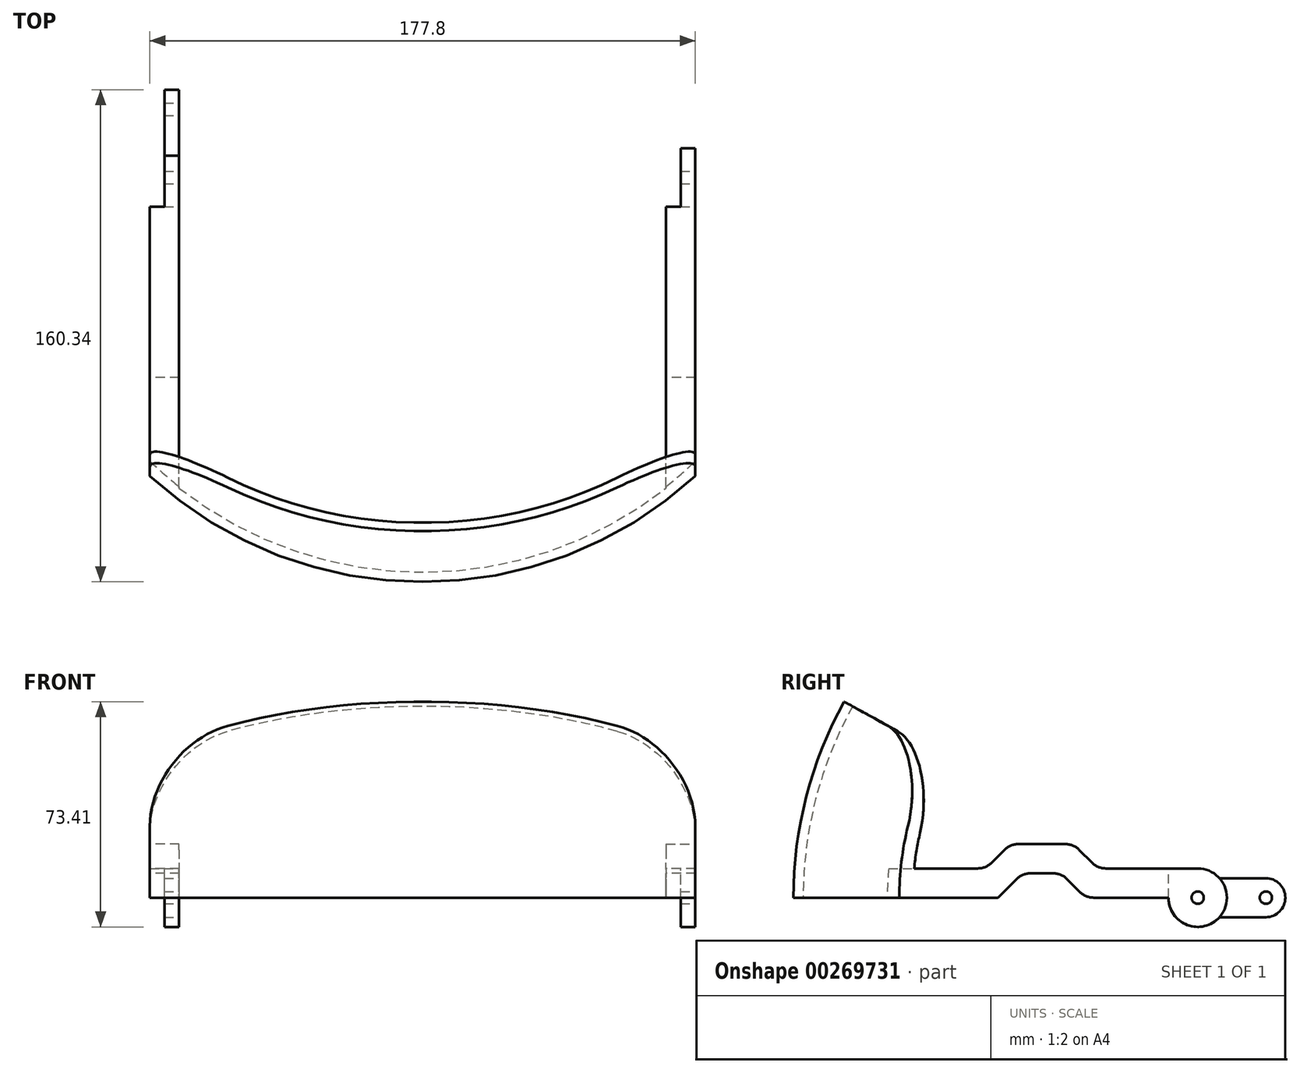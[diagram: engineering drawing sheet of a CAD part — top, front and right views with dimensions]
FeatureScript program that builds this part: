
annotation { "Feature Type Name" : "Feature", "Feature Type Description" : "" }
export const myFeature = defineFeature(function(context is Context, id is Id, definition is map)
    precondition{}
    {
        {
            var Q0;
            Q0=qCreatedBy(makeId("Right.planeOp"),FACE);
            var sketch = newSketch(context, id + "F0", { "sketchPlane" : qUnion([Q0])});
            skArc(sketch, "E0", {"start": v(0, 131.76) * mm, "mid": v(-131.76, 0) * mm, "end": v(0, -131.76) * mm});
            skArc(sketch, "E1", {"start": v(0, 128.59) * mm, "mid": v(-128.59, 0) * mm, "end": v(0, -128.59) * mm});
            skLineSegment(sketch, "E2", {"start": v(0, 131.76) * mm, "end": v(0, 128.59) * mm});
            skLineSegment(sketch, "E3.trimOffspring", {"start": v(0, 0) * mm, "end": v(0, -131.76) * mm});
            skPoint(sketch, "E4.orphan", {"position": v(0, 135.47) * mm});
            skSolve(sketch);
        }
        {
            var Q0;
            Q0 = qSketchRegion(id + "F0", true);
            var Q1;
            Q1=sQuery(id+"F0.wireOp",EDGE,"E3.trimOffspring");
            revolve(context, id + "F1", {"entities" : qUnion([Q0]), "axis" : qUnion([Q1]), "revolveType" : RevolveType.FULL});
        }
        {
            var Q0;
            Q0=qCreatedBy(makeId("Front.planeOp"),FACE);
            var sketch = newSketch(context, id + "F2", { "sketchPlane" : qUnion([Q0])});
            skLineSegment(sketch, "E5.left", {"start": v(88.9, 152.6) * mm, "end": v(88.9, -152.6) * mm});
            skLineSegment(sketch, "E5.right", {"start": v(-88.9, 152.6) * mm, "end": v(-88.9, -152.6) * mm});
            skPoint(sketch, "E5.middle", {"position": v(0, 0) * mm});
            skLineSegment(sketch, "E6.bottom", {"start": v(230.94, 152.6) * mm, "end": v(88.9, 152.6) * mm});
            skLineSegment(sketch, "E6.top", {"start": v(230.94, -152.6) * mm, "end": v(88.9, -152.6) * mm});
            skLineSegment(sketch, "E6.left", {"start": v(230.94, 152.6) * mm, "end": v(230.94, -152.6) * mm});
            skLineSegment(sketch, "E6.right", {"start": v(-230.94, 152.6) * mm, "end": v(-230.94, -152.6) * mm});
            skLineSegment(sketch, "E7.trimOffspring", {"start": v(-88.9, 152.6) * mm, "end": v(-230.94, 152.6) * mm});
            skPoint(sketch, "E5.bottom.start.orphan", {"position": v(88.9, 254.33) * mm});
            skPoint(sketch, "E8.orphan", {"position": v(-88.9, 254.33) * mm});
            skLineSegment(sketch, "E9.trimOffspring", {"start": v(-88.9, -152.6) * mm, "end": v(-230.94, -152.6) * mm});
            skPoint(sketch, "E5.top.end.orphan", {"position": v(-88.9, -254.33) * mm});
            skPoint(sketch, "E5.top.start.orphan", {"position": v(88.9, -254.33) * mm});
            skSolve(sketch);
        }
        {
            var Q0;
            Q0 = qSketchRegion(id + "F2", true);
            extrude(context, id + "F3", {"entities" : qUnion([Q0]), "operationType" : NewBodyOperationType.REMOVE, "endBound" : BoundingType.SYMMETRIC, "oppositeDirection" : true, "depth" : 304.8 * mm});
        }
        {
            var Q0;
            Q0=qCreatedBy(makeId("Right.planeOp"),FACE);
            var sketch = newSketch(context, id + "F4", { "sketchPlane" : qUnion([Q0])});
            skLineSegment(sketch, "E10", {"start": v(0, 0) * mm, "end": v(-147.9, 0) * mm});
            skLineSegment(sketch, "E11", {"start": v(0, 0) * mm, "end": v(-129.35, 71.7) * mm});
            skArc(sketch, "E12", {"start": v(-147.9, 0) * mm, "mid": v(143.19, -37.03) * mm, "end": v(-129.35, 71.7) * mm});
            skSolve(sketch);
        }
        {
            var Q0;
            Q0 = qSketchRegion(id + "F4", true);
            extrude(context, id + "F5", {"entities" : qUnion([Q0]), "operationType" : NewBodyOperationType.REMOVE, "endBound" : BoundingType.SYMMETRIC, "depth" : 304.8 * mm});
        }
        {
            var Q0;
            Q0=makeQuery(id+"F5.boolean.opBoolean","INTERSECT",EDGE,{"derivedFrom":[makeQuery(id+"F3.boolean.opBoolean","COPY",FACE,{"derivedFrom":makeQuery(id+"F3.opExtrude","SWEPT_FACE",FACE,{"disambiguationData":[OSD([sQuery(id+"F2.wireOp",EDGE,"E5.left")])]})}),makeQuery(id+"F5.opExtrude","SWEPT_FACE",FACE,{"disambiguationData":[OSD([sQuery(id+"F4.wireOp",EDGE,"E11")])]})]});
            var Q1;
            Q1=makeQuery(id+"F5.boolean.opBoolean","INTERSECT",EDGE,{"derivedFrom":[makeQuery(id+"F3.boolean.opBoolean","COPY",FACE,{"derivedFrom":makeQuery(id+"F3.opExtrude","SWEPT_FACE",FACE,{"disambiguationData":[OSD([sQuery(id+"F2.wireOp",EDGE,"E5.right")])]})}),makeQuery(id+"F5.opExtrude","SWEPT_FACE",FACE,{"disambiguationData":[OSD([sQuery(id+"F4.wireOp",EDGE,"E11")])]})]});
            fillet(context, id + "F6", {"entities" : qUnion([Q0, Q1]), "radius" : 25.4 * mm, "tangentPropagation" : true, "allowEdgeOverflow" : false});
        }
        {
            var Q0;
            Q0=qCreatedBy(makeId("Front.planeOp"),FACE);
            var sketch = newSketch(context, id + "F7", { "sketchPlane" : qUnion([Q0])});
            skLineSegment(sketch, "E13", {"start": v(88.9, 0) * mm, "end": v(79.38, 0) * mm});
            skLineSegment(sketch, "E14", {"start": v(88.9, 0) * mm, "end": v(88.9, 9.52) * mm});
            skLineSegment(sketch, "E15", {"start": v(-88.9, 0) * mm, "end": v(-88.9, 9.52) * mm});
            skLineSegment(sketch, "E16", {"start": v(88.9, 9.52) * mm, "end": v(79.38, 9.52) * mm});
            skLineSegment(sketch, "E17", {"start": v(79.38, 9.52) * mm, "end": v(79.38, 0) * mm});
            skLineSegment(sketch, "E18", {"start": v(-79.38, 9.52) * mm, "end": v(-79.38, 0) * mm});
            skLineSegment(sketch, "E19.trimOffspring", {"start": v(-79.38, 9.52) * mm, "end": v(-88.9, 9.52) * mm});
            skLineSegment(sketch, "E20.trimOffspring", {"start": v(-79.38, 0) * mm, "end": v(-88.9, 0) * mm});
            skPoint(sketch, "E21.orphan", {"position": v(-88.9, 10) * mm});
            skPoint(sketch, "E22.orphan", {"position": v(94.46, 0) * mm});
            skSolve(sketch);
        }
        {
            var Q0;
            Q0 = qSketchRegion(id + "F7", true);
            var Q1;
            Q1=makeQuery(id+"F1.opRevolve","SWEPT_FACE",FACE,{"disambiguationData":[OSD([sQuery(id+"F0.wireOp",EDGE,"E1")])]});
            extrude(context, id + "F8", {"entities" : qUnion([Q0]), "operationType" : NewBodyOperationType.ADD, "endBound" : BoundingType.UP_TO_SURFACE, "endBoundEntityFace" : qUnion([Q1]), "depth" : 25.4 * mm});
        }
        {
            var Q0;
            Q0=makeQuery(id+"F8.boolean.opBoolean","MERGE",FACE,{"derivedFrom":[makeQuery(id+"F3.boolean.opBoolean","COPY",FACE,{"derivedFrom":makeQuery(id+"F3.opExtrude","SWEPT_FACE",FACE,{"disambiguationData":[OSD([sQuery(id+"F2.wireOp",EDGE,"E5.left")])]})}),makeQuery(id+"F8.opExtrude","SWEPT_FACE",FACE,{"disambiguationData":[OSD([sQuery(id+"F7.wireOp",EDGE,"E14")])]})]});
            var sketch = newSketch(context, id + "F9", { "sketchPlane" : qUnion([Q0])});
            skLineSegment(sketch, "E23", {"start": v(-23.04, 0) * mm, "end": v(-36.51, 0) * mm});
            skPoint(sketch, "E24.endSnap0", {"position": v(0, 4.76) * mm});
            skLineSegment(sketch, "E25", {"start": v(-40.5, 17.46) * mm, "end": v(-61.1, 17.46) * mm});
            skLineSegment(sketch, "E26", {"start": v(-41.28, 17.46) * mm, "end": v(-41.28, 4.76) * mm});
            skLineSegment(sketch, "E27", {"start": v(-60.33, 17.46) * mm, "end": v(-60.33, 4.76) * mm});
            skLineSegment(sketch, "E28", {"start": v(-70.62, 7.94) * mm, "end": v(-30.98, 7.94) * mm});
            skPoint(sketch, "E29.orphan", {"position": v(-87.84, 4.76) * mm});
            skLineSegment(sketch, "E30", {"start": v(-60.33, 4.76) * mm, "end": v(-57.15, 7.94) * mm});
            skLineSegment(sketch, "E31", {"start": v(-41.28, 4.76) * mm, "end": v(-44.45, 7.94) * mm});
            skLineSegment(sketch, "E32", {"start": v(-60.32, 4.76) * mm, "end": v(-65.09, 0) * mm});
            skLineSegment(sketch, "E33", {"start": v(-41.28, 4.76) * mm, "end": v(-36.51, 0) * mm});
            skPoint(sketch, "E34.start.orphan", {"position": v(0, 19.8) * mm});
            skLineSegment(sketch, "E35", {"start": v(-61.1, 17.46) * mm, "end": v(-78.56, 0) * mm});
            skLineSegment(sketch, "E36", {"start": v(-40.5, 17.46) * mm, "end": v(-23.04, 0) * mm});
            skPoint(sketch, "E37.orphan", {"position": v(0, 17.46) * mm});
            skLineSegment(sketch, "E38.trimOffspring", {"start": v(-65.09, 0) * mm, "end": v(-78.56, 0) * mm});
            skSolve(sketch);
        }
        {
            var Q0;
            Q0 = qSketchRegion(id + "F9", true);
            extrude(context, id + "F10", {"entities" : qUnion([Q0]), "operationType" : NewBodyOperationType.ADD, "oppositeDirection" : true, "depth" : 9.52 * mm});
        }
        {
            var Q0;
            Q0=makeQuery(id+"F8.boolean.opBoolean","MERGE",FACE,{"derivedFrom":[makeQuery(id+"F3.boolean.opBoolean","COPY",FACE,{"derivedFrom":makeQuery(id+"F3.opExtrude","SWEPT_FACE",FACE,{"disambiguationData":[OSD([sQuery(id+"F2.wireOp",EDGE,"E5.right")])]})}),makeQuery(id+"F8.opExtrude","SWEPT_FACE",FACE,{"disambiguationData":[OSD([sQuery(id+"F7.wireOp",EDGE,"E15")])]})]});
            var sketch = newSketch(context, id + "F11", { "sketchPlane" : qUnion([Q0])});
            skLineSegment(sketch, "E39", {"start": v(40.5, 17.46) * mm, "end": v(61.1, 17.46) * mm});
            skLineSegment(sketch, "E40", {"start": v(41.28, 7.94) * mm, "end": v(41.28, 0) * mm});
            skLineSegment(sketch, "E41", {"start": v(60.33, 7.94) * mm, "end": v(60.33, 0) * mm});
            skLineSegment(sketch, "E42", {"start": v(41.28, 0) * mm, "end": v(60.33, 0) * mm});
            skLineSegment(sketch, "E43", {"start": v(41.28, 4.76) * mm, "end": v(44.45, 7.94) * mm});
            skLineSegment(sketch, "E44", {"start": v(60.33, 4.76) * mm, "end": v(55.56, 9.53) * mm});
            skLineSegment(sketch, "E45", {"start": v(30.98, 7.94) * mm, "end": v(41.28, 7.94) * mm});
            skLineSegment(sketch, "E46", {"start": v(40.5, 17.46) * mm, "end": v(30.98, 7.94) * mm});
            skLineSegment(sketch, "E47", {"start": v(61.1, 17.46) * mm, "end": v(70.62, 7.94) * mm});
            skPoint(sketch, "E48.orphan", {"position": v(41.28, 9.52) * mm});
            skLineSegment(sketch, "E49.trimOffspring", {"start": v(60.33, 7.94) * mm, "end": v(70.62, 7.94) * mm});
            skPoint(sketch, "E50.orphan", {"position": v(60.33, 9.52) * mm});
            skSolve(sketch);
        }
        {
            var Q0;
            Q0 = qSketchRegion(id + "F11", true);
            extrude(context, id + "F12", {"entities" : qUnion([Q0]), "operationType" : NewBodyOperationType.ADD, "oppositeDirection" : true, "depth" : 9.52 * mm});
        }
        {
            var Q0;
            Q0=qCreatedBy(makeId("Right.planeOp"),FACE);
            var sketch = newSketch(context, id + "F13", { "sketchPlane" : qUnion([Q0])});
            skLineSegment(sketch, "E51", {"start": v(-36.51, 0) * mm, "end": v(-65.09, 0) * mm});
            skLineSegment(sketch, "E52", {"start": v(-44.45, 7.94) * mm, "end": v(-57.15, 7.94) * mm});
            skLineSegment(sketch, "E53", {"start": v(-60.33, 7.94) * mm, "end": v(-60.33, 4.76) * mm});
            skLineSegment(sketch, "E54.trimOffspring", {"start": v(-41.28, 4.76) * mm, "end": v(-41.28, 7.94) * mm});
            skLineSegment(sketch, "E55", {"start": v(-60.33, 4.76) * mm, "end": v(-57.15, 7.94) * mm});
            skLineSegment(sketch, "E56", {"start": v(-41.28, 4.76) * mm, "end": v(-44.45, 7.94) * mm});
            skLineSegment(sketch, "E57", {"start": v(-60.33, 4.76) * mm, "end": v(-65.09, 0) * mm});
            skLineSegment(sketch, "E58", {"start": v(-41.28, 4.76) * mm, "end": v(-36.51, 0) * mm});
            skSolve(sketch);
        }
        {
            var Q0;
            Q0 = qSketchRegion(id + "F13", true);
            extrude(context, id + "F14", {"entities" : qUnion([Q0]), "operationType" : NewBodyOperationType.REMOVE, "endBound" : BoundingType.SYMMETRIC, "depth" : 177.8 * mm});
        }
        {
            var Q0;
            Q0=makeQuery(id+"F9Fqv3LpDGS5zFg_1.boolean.opBoolean","MERGE",FACE,{"derivedFrom":[makeQuery(id+"F8.boolean.opBoolean","MERGE",FACE,{"derivedFrom":[makeQuery(id+"F3.boolean.opBoolean","COPY",FACE,{"derivedFrom":makeQuery(id+"F3.opExtrude","SWEPT_FACE",FACE,{"disambiguationData":[OSD([sQuery(id+"F2.wireOp",EDGE,"E5.left")])]})}),makeQuery(id+"F8.opExtrude","SWEPT_FACE",FACE,{"disambiguationData":[OSD([sQuery(id+"F7.wireOp",EDGE,"E14")])]})]}),makeQuery(id+"F9Fqv3LpDGS5zFg_1.opExtrude","CAP_FACE",FACE,{"disambiguationData":[OSD([sQuery(id+"Fdyxyt73cwK6mQ5_1.wireOp",EDGE,"uge7HxcK-xsYJ-EXUT-pD71-h3y1mwA4NyrV"),sQuery(id+"Fdyxyt73cwK6mQ5_1.wireOp",EDGE,"hfxr85zl-CjJz-dNnQ-cUyG-KzP6Vcheir9o"),sQuery(id+"Fdyxyt73cwK6mQ5_1.wireOp",EDGE,"DYdveK2D-yC2o-hGCK-GH33-UXKGGb30pmTF"),sQuery(id+"Fdyxyt73cwK6mQ5_1.wireOp",EDGE,"KyHsQCAR-jBkV-1PyX-yX3m-mguW6c5BXjM3"),sQuery(id+"Fdyxyt73cwK6mQ5_1.wireOp",EDGE,"KXiKUkZQ-NJSx-R7BF-pjD5-MABOeaKY5b3t"),sQuery(id+"Fdyxyt73cwK6mQ5_1.wireOp",EDGE,"uAoFoTMZ-oCW3-4zug-ka1U-f82iXX2Ucrwf"),sQuery(id+"Fdyxyt73cwK6mQ5_1.wireOp",EDGE,"oFfLLbmo-RIOd-E5QO-eRZp-mn8jqRh1hiLr"),sQuery(id+"Fdyxyt73cwK6mQ5_1.wireOp",EDGE,"XboE2R6W-MqqC-2Aew-ZZfI-9xdbT96ioL7k"),sQuery(id+"Fdyxyt73cwK6mQ5_1.wireOp",EDGE,"il7hj7Cw-iAn3-ZAEo-7ila-wyK5fjaZt0oG"),sQuery(id+"Fdyxyt73cwK6mQ5_1.wireOp",EDGE,"2c3155a9-a74c-4d56-af0e-1345a1cb9d5a.trimOffspring")])],"isStart":true})]});
            var sketch = newSketch(context, id + "F15", { "sketchPlane" : qUnion([Q0])});
            skCircle(sketch, "E59", {"center": v(0, 0) * mm, "radius": 9.52 * mm});
            skSolve(sketch);
        }
        {
            var Q0;
            Q0 = qSketchRegion(id + "F15", true);
            extrude(context, id + "F16", {"entities" : qUnion([Q0]), "operationType" : NewBodyOperationType.ADD, "oppositeDirection" : true, "depth" : 4.76 * mm});
        }
        {
            var Q0;
            Q0=makeQuery(id+"F12.boolean.opBoolean","MERGE",FACE,{"derivedFrom":[makeQuery(id+"F8.opExtrude","SWEPT_FACE",FACE,{"disambiguationData":[OSD([sQuery(id+"F7.wireOp",EDGE,"E18")])]}),makeQuery(id+"F12.opExtrude","CAP_FACE",FACE,{"disambiguationData":[OSD([sQuery(id+"F11.wireOp",EDGE,"E39"),sQuery(id+"F11.wireOp",EDGE,"E40"),sQuery(id+"F11.wireOp",EDGE,"E41"),sQuery(id+"F11.wireOp",EDGE,"E42"),sQuery(id+"F11.wireOp",EDGE,"E45"),sQuery(id+"F11.wireOp",EDGE,"E46"),sQuery(id+"F11.wireOp",EDGE,"E47"),sQuery(id+"F11.wireOp",EDGE,"E49.trimOffspring")])],"isStart":false})]});
            var sketch = newSketch(context, id + "F17", { "sketchPlane" : qUnion([Q0])});
            skCircle(sketch, "E60", {"center": v(0, 0) * mm, "radius": 9.52 * mm});
            skSolve(sketch);
        }
        {
            var Q0;
            Q0 = qSketchRegion(id + "F17", true);
            extrude(context, id + "F18", {"entities" : qUnion([Q0]), "operationType" : NewBodyOperationType.ADD, "oppositeDirection" : true, "depth" : 4.76 * mm});
        }
        {
            var Q0;
            Q0=qCreatedBy(makeId("Right.planeOp"),FACE);
            var sketch = newSketch(context, id + "F19", { "sketchPlane" : qUnion([Q0])});
            skCircle(sketch, "E61", {"center": v(0, 0) * mm, "radius": 2 * mm});
            skSolve(sketch);
        }
        {
            var Q0;
            Q0 = qSketchRegion(id + "F19", true);
            extrude(context, id + "F20", {"entities" : qUnion([Q0]), "operationType" : NewBodyOperationType.REMOVE, "endBound" : BoundingType.SYMMETRIC, "oppositeDirection" : true, "depth" : 177.8 * mm});
        }
        {
            var Q0;
            Q0=makeQuery(id+"F12.boolean.opBoolean","MERGE",FACE,{"derivedFrom":[makeQuery(id+"F8.boolean.opBoolean","MERGE",FACE,{"derivedFrom":[makeQuery(id+"F3.boolean.opBoolean","COPY",FACE,{"derivedFrom":makeQuery(id+"F3.opExtrude","SWEPT_FACE",FACE,{"disambiguationData":[OSD([sQuery(id+"F2.wireOp",EDGE,"E5.right")])]})}),makeQuery(id+"F8.opExtrude","SWEPT_FACE",FACE,{"disambiguationData":[OSD([sQuery(id+"F7.wireOp",EDGE,"E15")])]})]}),makeQuery(id+"F12.opExtrude","CAP_FACE",FACE,{"disambiguationData":[OSD([sQuery(id+"F11.wireOp",EDGE,"E39"),sQuery(id+"F11.wireOp",EDGE,"E40"),sQuery(id+"F11.wireOp",EDGE,"E41"),sQuery(id+"F11.wireOp",EDGE,"E42"),sQuery(id+"F11.wireOp",EDGE,"E45"),sQuery(id+"F11.wireOp",EDGE,"E46"),sQuery(id+"F11.wireOp",EDGE,"E47"),sQuery(id+"F11.wireOp",EDGE,"E49.trimOffspring")])],"isStart":true})]});
            var sketch = newSketch(context, id + "F21", { "sketchPlane" : qUnion([Q0])});
            skArc(sketch, "E62", {"start": v(0, 9.52) * mm, "mid": v(-6.74, -6.74) * mm, "end": v(9.52, 0) * mm});
            skLineSegment(sketch, "E63", {"start": v(9.52, 0) * mm, "end": v(9.52, 9.52) * mm});
            skLineSegment(sketch, "E64", {"start": v(9.52, 9.52) * mm, "end": v(0, 9.52) * mm});
            skSolve(sketch);
        }
        {
            var Q0;
            Q0 = qSketchRegion(id + "F21", true);
            extrude(context, id + "F22", {"entities" : qUnion([Q0]), "operationType" : NewBodyOperationType.REMOVE, "oppositeDirection" : true, "depth" : 4.76 * mm});
        }
        {
            var Q0;
            Q0=makeQuery(id+"F9Fqv3LpDGS5zFg_1.boolean.opBoolean","MERGE",FACE,{"derivedFrom":[makeQuery(id+"F8.opExtrude","SWEPT_FACE",FACE,{"disambiguationData":[OSD([sQuery(id+"F7.wireOp",EDGE,"E17")])]}),makeQuery(id+"F9Fqv3LpDGS5zFg_1.opExtrude","CAP_FACE",FACE,{"disambiguationData":[OSD([sQuery(id+"Fdyxyt73cwK6mQ5_1.wireOp",EDGE,"uge7HxcK-xsYJ-EXUT-pD71-h3y1mwA4NyrV"),sQuery(id+"Fdyxyt73cwK6mQ5_1.wireOp",EDGE,"hfxr85zl-CjJz-dNnQ-cUyG-KzP6Vcheir9o"),sQuery(id+"Fdyxyt73cwK6mQ5_1.wireOp",EDGE,"DYdveK2D-yC2o-hGCK-GH33-UXKGGb30pmTF"),sQuery(id+"Fdyxyt73cwK6mQ5_1.wireOp",EDGE,"KyHsQCAR-jBkV-1PyX-yX3m-mguW6c5BXjM3"),sQuery(id+"Fdyxyt73cwK6mQ5_1.wireOp",EDGE,"KXiKUkZQ-NJSx-R7BF-pjD5-MABOeaKY5b3t"),sQuery(id+"Fdyxyt73cwK6mQ5_1.wireOp",EDGE,"uAoFoTMZ-oCW3-4zug-ka1U-f82iXX2Ucrwf"),sQuery(id+"Fdyxyt73cwK6mQ5_1.wireOp",EDGE,"oFfLLbmo-RIOd-E5QO-eRZp-mn8jqRh1hiLr"),sQuery(id+"Fdyxyt73cwK6mQ5_1.wireOp",EDGE,"XboE2R6W-MqqC-2Aew-ZZfI-9xdbT96ioL7k"),sQuery(id+"Fdyxyt73cwK6mQ5_1.wireOp",EDGE,"il7hj7Cw-iAn3-ZAEo-7ila-wyK5fjaZt0oG"),sQuery(id+"Fdyxyt73cwK6mQ5_1.wireOp",EDGE,"2c3155a9-a74c-4d56-af0e-1345a1cb9d5a.trimOffspring")])],"isStart":false})]});
            var sketch = newSketch(context, id + "F23", { "sketchPlane" : qUnion([Q0])});
            skArc(sketch, "E65", {"start": v(0, 9.52) * mm, "mid": v(-6.74, -6.74) * mm, "end": v(9.52, 0) * mm});
            skLineSegment(sketch, "E66", {"start": v(9.52, 0) * mm, "end": v(9.52, 9.52) * mm});
            skLineSegment(sketch, "E67", {"start": v(9.52, 9.52) * mm, "end": v(0, 9.52) * mm});
            skSolve(sketch);
        }
        {
            var Q0;
            Q0 = qSketchRegion(id + "F23", true);
            extrude(context, id + "F24", {"entities" : qUnion([Q0]), "operationType" : NewBodyOperationType.REMOVE, "oppositeDirection" : true, "depth" : 4.76 * mm});
        }
        {
            var Q0;
            Q0=makeQuery(id+"F8.opExtrude","TWEAK_EDGE",EDGE,{"derivedFrom":[makeQuery(id+"F1.opRevolve","SWEPT_FACE",FACE,{"disambiguationData":[OSD([sQuery(id+"F0.wireOp",EDGE,"E1")])]}),makeQuery(id+"F7.imprint","IMPRINT",EDGE,{"derivedFrom":sQuery(id+"F7.wireOp",EDGE,"E19.trimOffspring")})]});
            var Q1;
            Q1=makeQuery(id+"F8.opExtrude","TWEAK_EDGE",EDGE,{"derivedFrom":[makeQuery(id+"F1.opRevolve","SWEPT_FACE",FACE,{"disambiguationData":[OSD([sQuery(id+"F0.wireOp",EDGE,"E1")])]}),makeQuery(id+"F7.imprint","IMPRINT",EDGE,{"derivedFrom":sQuery(id+"F7.wireOp",EDGE,"E16")})]});
            var Q2;
            Q2=makeQuery(id+"F24.boolean.opBoolean","COPY",EDGE,{"derivedFrom":makeQuery(id+"F24.opExtrude","CAP_EDGE",EDGE,{"disambiguationData":[OSD([sQuery(id+"F23.wireOp",EDGE,"E66")])],"isStart":true})});
            var Q3;
            Q3=makeQuery(id+"F10.boolean.opBoolean","INTERSECT",EDGE,{"derivedFrom":[makeQuery(id+"F8.opExtrude","SWEPT_FACE",FACE,{"disambiguationData":[OSD([sQuery(id+"F7.wireOp",EDGE,"E16")])]}),makeQuery(id+"F10.opExtrude","SWEPT_FACE",FACE,{"disambiguationData":[OSD([sQuery(id+"F9.wireOp",EDGE,"E36")])]})]});
            var Q4;
            Q4=makeQuery(id+"F10.opExtrude","SWEPT_EDGE",EDGE,{"disambiguationData":[OSD([sQuery(id+"F9.wireOp",EDGE,"E25"),sQuery(id+"F9.wireOp",EDGE,"E36")])]});
            var Q5;
            Q5=makeQuery(id+"F10.opExtrude","SWEPT_EDGE",EDGE,{"disambiguationData":[OSD([sQuery(id+"F9.wireOp",EDGE,"E25"),sQuery(id+"F9.wireOp",EDGE,"E35")])]});
            var Q6;
            Q6=makeQuery(id+"F10.boolean.opBoolean","INTERSECT",EDGE,{"derivedFrom":[makeQuery(id+"F8.opExtrude","SWEPT_FACE",FACE,{"disambiguationData":[OSD([sQuery(id+"F7.wireOp",EDGE,"E16")])]}),makeQuery(id+"F10.opExtrude","SWEPT_FACE",FACE,{"disambiguationData":[OSD([sQuery(id+"F9.wireOp",EDGE,"E35")])]})]});
            var Q7;
            Q7=makeQuery(id+"F12.boolean.opBoolean","INTERSECT",EDGE,{"derivedFrom":[makeQuery(id+"F8.opExtrude","SWEPT_FACE",FACE,{"disambiguationData":[OSD([sQuery(id+"F7.wireOp",EDGE,"E19.trimOffspring")])]}),makeQuery(id+"F12.opExtrude","SWEPT_FACE",FACE,{"disambiguationData":[OSD([sQuery(id+"F11.wireOp",EDGE,"E46")])]})]});
            var Q8;
            Q8=makeQuery(id+"F12.opExtrude","SWEPT_EDGE",EDGE,{"disambiguationData":[OSD([sQuery(id+"F11.wireOp",EDGE,"E39"),sQuery(id+"F11.wireOp",EDGE,"E46")])]});
            var Q9;
            Q9=makeQuery(id+"F12.opExtrude","SWEPT_EDGE",EDGE,{"disambiguationData":[OSD([sQuery(id+"F11.wireOp",EDGE,"E39"),sQuery(id+"F11.wireOp",EDGE,"E47")])]});
            var Q10;
            Q10=makeQuery(id+"F12.boolean.opBoolean","INTERSECT",EDGE,{"derivedFrom":[makeQuery(id+"F8.opExtrude","SWEPT_FACE",FACE,{"disambiguationData":[OSD([sQuery(id+"F7.wireOp",EDGE,"E19.trimOffspring")])]}),makeQuery(id+"F12.opExtrude","SWEPT_FACE",FACE,{"disambiguationData":[OSD([sQuery(id+"F11.wireOp",EDGE,"E47")])]})]});
            var Q11;
            {var subQ10=sQuery(id+"F13.wireOp",EDGE,"E58");Q11=makeQuery(id+"F14.boolean.opBoolean","COPY",EDGE,{"disambiguationData":[TD([makeQuery(id+"F3.boolean.opBoolean","COPY",FACE,{"derivedFrom":makeQuery(id+"F3.opExtrude","SWEPT_FACE",FACE,{"disambiguationData":[OSD([sQuery(id+"F2.wireOp",EDGE,"E5.left")])]})})])],"derivedFrom":makeQuery(id+"F14.opExtrude","SWEPT_EDGE",EDGE,{"disambiguationData":[OSD([sQuery(id+"F13.wireOp",EDGE,"E51"),subQ10])]})});}
            var Q12;
            {var subQ10=sQuery(id+"F13.wireOp",EDGE,"E57");Q12=makeQuery(id+"F14.boolean.opBoolean","COPY",EDGE,{"disambiguationData":[TD([makeQuery(id+"F3.boolean.opBoolean","COPY",FACE,{"derivedFrom":makeQuery(id+"F3.opExtrude","SWEPT_FACE",FACE,{"disambiguationData":[OSD([sQuery(id+"F2.wireOp",EDGE,"E5.left")])]})})])],"derivedFrom":makeQuery(id+"F14.opExtrude","SWEPT_EDGE",EDGE,{"disambiguationData":[OSD([sQuery(id+"F13.wireOp",EDGE,"E51"),subQ10])]})});}
            var Q13;
            {var subQ10=sQuery(id+"F13.wireOp",EDGE,"E52");var subQ11=sQuery(id+"F13.wireOp",EDGE,"E55");Q13=makeQuery(id+"F14.boolean.opBoolean","COPY",EDGE,{"disambiguationData":[TD([makeQuery(id+"F3.boolean.opBoolean","COPY",FACE,{"derivedFrom":makeQuery(id+"F3.opExtrude","SWEPT_FACE",FACE,{"disambiguationData":[OSD([sQuery(id+"F2.wireOp",EDGE,"E5.left")])]})})])],"derivedFrom":makeQuery(id+"F14.opExtrude","SWEPT_EDGE",EDGE,{"disambiguationData":[OSD([subQ10,subQ11])]})});}
            var Q14;
            {var subQ10=sQuery(id+"F13.wireOp",EDGE,"E56");var subQ11=sQuery(id+"F13.wireOp",EDGE,"E52");Q14=makeQuery(id+"F14.boolean.opBoolean","COPY",EDGE,{"disambiguationData":[TD([makeQuery(id+"F3.boolean.opBoolean","COPY",FACE,{"derivedFrom":makeQuery(id+"F3.opExtrude","SWEPT_FACE",FACE,{"disambiguationData":[OSD([sQuery(id+"F2.wireOp",EDGE,"E5.left")])]})})])],"derivedFrom":makeQuery(id+"F14.opExtrude","SWEPT_EDGE",EDGE,{"disambiguationData":[OSD([subQ11,subQ10])]})});}
            var Q15;
            {var subQ8=sQuery(id+"F13.wireOp",EDGE,"E57");Q15=makeQuery(id+"F14.boolean.opBoolean","COPY",EDGE,{"disambiguationData":[TD([makeQuery(id+"F3.boolean.opBoolean","COPY",FACE,{"derivedFrom":makeQuery(id+"F3.opExtrude","SWEPT_FACE",FACE,{"disambiguationData":[OSD([sQuery(id+"F2.wireOp",EDGE,"E5.right")])]})})])],"derivedFrom":makeQuery(id+"F14.opExtrude","SWEPT_EDGE",EDGE,{"disambiguationData":[OSD([sQuery(id+"F13.wireOp",EDGE,"E51"),subQ8])]})});}
            var Q16;
            {var subQ8=sQuery(id+"F13.wireOp",EDGE,"E52");var subQ9=sQuery(id+"F13.wireOp",EDGE,"E55");Q16=makeQuery(id+"F14.boolean.opBoolean","COPY",EDGE,{"disambiguationData":[TD([makeQuery(id+"F3.boolean.opBoolean","COPY",FACE,{"derivedFrom":makeQuery(id+"F3.opExtrude","SWEPT_FACE",FACE,{"disambiguationData":[OSD([sQuery(id+"F2.wireOp",EDGE,"E5.right")])]})})])],"derivedFrom":makeQuery(id+"F14.opExtrude","SWEPT_EDGE",EDGE,{"disambiguationData":[OSD([subQ8,subQ9])]})});}
            var Q17;
            {var subQ8=sQuery(id+"F13.wireOp",EDGE,"E52");var subQ9=sQuery(id+"F13.wireOp",EDGE,"E56");Q17=makeQuery(id+"F14.boolean.opBoolean","COPY",EDGE,{"disambiguationData":[TD([makeQuery(id+"F3.boolean.opBoolean","COPY",FACE,{"derivedFrom":makeQuery(id+"F3.opExtrude","SWEPT_FACE",FACE,{"disambiguationData":[OSD([sQuery(id+"F2.wireOp",EDGE,"E5.right")])]})})])],"derivedFrom":makeQuery(id+"F14.opExtrude","SWEPT_EDGE",EDGE,{"disambiguationData":[OSD([subQ8,subQ9])]})});}
            var Q18;
            {var subQ0=sQuery(id+"F13.wireOp",EDGE,"E58");Q18=makeQuery(id+"F14.boolean.opBoolean","COPY",EDGE,{"disambiguationData":[TD([makeQuery(id+"F3.boolean.opBoolean","COPY",FACE,{"derivedFrom":makeQuery(id+"F3.opExtrude","SWEPT_FACE",FACE,{"disambiguationData":[OSD([sQuery(id+"F2.wireOp",EDGE,"E5.right")])]})})])],"derivedFrom":makeQuery(id+"F14.opExtrude","SWEPT_EDGE",EDGE,{"disambiguationData":[OSD([sQuery(id+"F13.wireOp",EDGE,"E51"),subQ0])]})});}
            var Q19;
            Q19=makeQuery(id+"F22.boolean.opBoolean","COPY",EDGE,{"derivedFrom":makeQuery(id+"F22.opExtrude","CAP_EDGE",EDGE,{"disambiguationData":[OSD([sQuery(id+"F21.wireOp",EDGE,"E63")])],"isStart":true})});
            fillet(context, id + "F25", {"entities" : qUnion([Q0, Q1, Q2, Q3, Q4, Q5, Q6, Q7, Q8, Q9, Q10, Q11, Q12, Q13, Q14, Q15, Q16, Q17, Q18, Q19]), "radius" : 6.35 * mm, "tangentPropagation" : true, "allowEdgeOverflow" : false});
        }
        {
            var Q0;
            Q0=makeQuery(id+"F18.boolean.opBoolean","MERGE",FACE,{"derivedFrom":[makeQuery(id+"F12.boolean.opBoolean","MERGE",FACE,{"derivedFrom":[makeQuery(id+"F8.opExtrude","SWEPT_FACE",FACE,{"disambiguationData":[OSD([sQuery(id+"F7.wireOp",EDGE,"E18")])]}),makeQuery(id+"F12.opExtrude","CAP_FACE",FACE,{"disambiguationData":[OSD([sQuery(id+"F11.wireOp",EDGE,"E39"),sQuery(id+"F11.wireOp",EDGE,"E40"),sQuery(id+"F11.wireOp",EDGE,"E41"),sQuery(id+"F11.wireOp",EDGE,"E42"),sQuery(id+"F11.wireOp",EDGE,"E45"),sQuery(id+"F11.wireOp",EDGE,"E46"),sQuery(id+"F11.wireOp",EDGE,"E47"),sQuery(id+"F11.wireOp",EDGE,"E49.trimOffspring")])],"isStart":false})]}),makeQuery(id+"F18.opExtrude","CAP_FACE",FACE,{"disambiguationData":[OSD([sQuery(id+"F17.wireOp",EDGE,"E60")])],"isStart":true})]});
            var sketch = newSketch(context, id + "F26", { "sketchPlane" : qUnion([Q0])});
            skArc(sketch, "E68", {"start": v(0, -2) * mm, "mid": v(2, 0) * mm, "end": v(0, 2) * mm});
            skLineSegment(sketch, "E69.bottom", {"start": v(22.22, 6.35) * mm, "end": v(0, 6.35) * mm});
            skLineSegment(sketch, "E69.top", {"start": v(22.23, -6.35) * mm, "end": v(0, -6.35) * mm});
            skLineSegment(sketch, "E70", {"start": v(0, 6.35) * mm, "end": v(0, 2) * mm});
            skPoint(sketch, "E71", {"position": v(22.22, 0) * mm});
            skArc(sketch, "E72", {"start": v(22.23, -6.35) * mm, "mid": v(28.58, 0) * mm, "end": v(22.22, 6.35) * mm});
            skPoint(sketch, "E69.right.end.orphan", {"position": v(-50.8, -6.35) * mm});
            skPoint(sketch, "E69.right.start.orphan", {"position": v(0, 6.35) * mm});
            skLineSegment(sketch, "E73.trimOffspring", {"start": v(0, -2) * mm, "end": v(0, -6.35) * mm});
            skPoint(sketch, "E74.orphan", {"position": v(0, 11.57) * mm});
            skPoint(sketch, "E75.orphan", {"position": v(50.8, 6.35) * mm});
            skPoint(sketch, "E76.orphan", {"position": v(0, -6.35) * mm});
            skPoint(sketch, "E77.orphan", {"position": v(25.4, 0) * mm});
            skCircle(sketch, "E78", {"center": v(22.22, 0) * mm, "radius": 2 * mm});
            skSolve(sketch);
        }
        {
            var Q0;
            Q0 = qSketchRegion(id + "F26", true);
            extrude(context, id + "F27", {"entities" : qUnion([Q0]), "operationType" : NewBodyOperationType.ADD, "oppositeDirection" : true, "depth" : 4.76 * mm});
        }
    });
